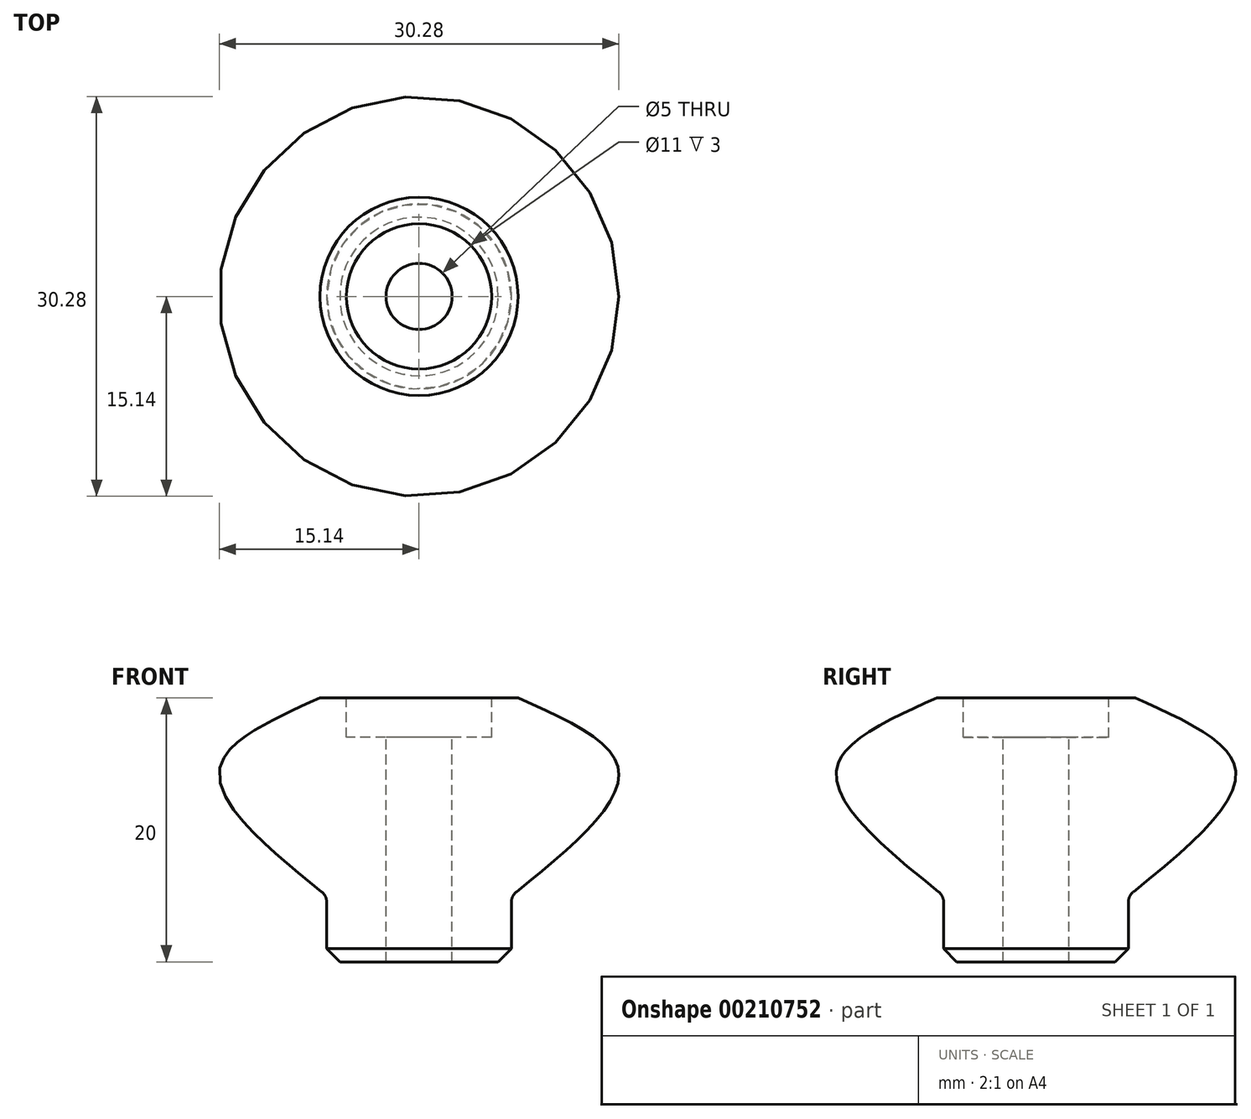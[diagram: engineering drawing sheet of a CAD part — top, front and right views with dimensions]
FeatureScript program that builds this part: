
annotation { "Feature Type Name" : "Feature", "Feature Type Description" : "" }
export const myFeature = defineFeature(function(context is Context, id is Id, definition is map)
    precondition{}
    {
        {
            var Q0;
            Q0=qCreatedBy(makeId("Top.planeOp"),FACE);
            var sketch = newSketch(context, id + "F0", { "sketchPlane" : qUnion([Q0])});
            skCircle(sketch, "E0", {"center": v(0, 0) * mm, "radius": 7 * mm});
            skSolve(sketch);
        }
        {
            var Q0;
            Q0 = qSketchRegion(id + "F0", true);
            extrude(context, id + "F1", {"entities" : qUnion([Q0]), "depth" : 5 * mm});
        }
        {
            var Q0;
            Q0=qCreatedBy(makeId("Top.planeOp"),FACE);
            cPlane(context, id + "F2", {"entities" : qUnion([Q0]), "cplaneType" : CPlaneType.OFFSET, "offset" : 20 * mm, "width" : 150 * mm, "height" : 150 * mm});
        }
        {
            var Q0;
            Q0=qCreatedBy(makeId("Top.planeOp"),FACE);
            cPlane(context, id + "F3", {"entities" : qUnion([Q0]), "cplaneType" : CPlaneType.OFFSET, "offset" : 15 * mm, "width" : 150 * mm, "height" : 150 * mm});
        }
        {
            var Q0;
            Q0=qCreatedBy(id+"F2.planeOp",FACE);
            var sketch = newSketch(context, id + "F4", { "sketchPlane" : qUnion([Q0])});
            skCircle(sketch, "E1", {"center": v(0, 0) * mm, "radius": 7.5 * mm});
            skSolve(sketch);
        }
        {
            var Q0;
            Q0=qCreatedBy(id+"F3.planeOp",FACE);
            var sketch = newSketch(context, id + "F5", { "sketchPlane" : qUnion([Q0])});
            skCircle(sketch, "E2", {"center": v(0, 0) * mm, "radius": 15 * mm});
            skSolve(sketch);
        }
        {
            var Q0;
            Q0=makeQuery(id+"F4.imprint","IMPRINT",FACE,{"disambiguationData":[TD([[makeQuery(id+"F4.imprint","IMPRINT",EDGE,{"derivedFrom":sQuery(id+"F4.wireOp",EDGE,"E1")}),1.0]])]});
            var Q1;
            Q1=makeQuery(id+"F5.imprint","IMPRINT",FACE,{"disambiguationData":[TD([[makeQuery(id+"F5.imprint","IMPRINT",EDGE,{"derivedFrom":sQuery(id+"F5.wireOp",EDGE,"E2")}),1.0]])]});
            var Q2;
            Q2=makeQuery(id+"F1.opExtrude","CAP_FACE",FACE,{"disambiguationData":[OSD([sQuery(id+"F0.wireOp",EDGE,"E0")])],"isStart":false});
            loft(context, id + "F6", {"operationType" : NewBodyOperationType.ADD, "sheetProfilesArray" : [{ "sheetProfileEntities" : qUnion([Q0]) }, { "sheetProfileEntities" : qUnion([Q1]) }, { "sheetProfileEntities" : qUnion([Q2]) }]});
        }
        {
            var Q0;
            Q0=makeQuery(id+"F4.imprint","IMPRINT",FACE,{"disambiguationData":[TD([[makeQuery(id+"F4.imprint","IMPRINT",EDGE,{"derivedFrom":sQuery(id+"F4.wireOp",EDGE,"E1")}),1.0]])]});
            var sketch = newSketch(context, id + "F7", { "sketchPlane" : qUnion([Q0])});
            skCircle(sketch, "E3", {"center": v(0, 0) * mm, "radius": 2.5 * mm});
            skSolve(sketch);
        }
        {
            var Q0;
            Q0 = qSketchRegion(id + "F7", true);
            extrude(context, id + "F8", {"entities" : qUnion([Q0]), "operationType" : NewBodyOperationType.REMOVE, "endBound" : BoundingType.THROUGH_ALL, "oppositeDirection" : true, "depth" : 25 * mm});
        }
        {
            var Q0;
            Q0=makeQuery(id+"F4.imprint","IMPRINT",FACE,{"disambiguationData":[TD([[makeQuery(id+"F4.imprint","IMPRINT",EDGE,{"derivedFrom":sQuery(id+"F4.wireOp",EDGE,"E1")}),1.0]])]});
            var sketch = newSketch(context, id + "F9", { "sketchPlane" : qUnion([Q0])});
            skCircle(sketch, "E4", {"center": v(0, 0) * mm, "radius": 5.5 * mm});
            skSolve(sketch);
        }
        {
            var Q0;
            Q0 = qSketchRegion(id + "F9", true);
            extrude(context, id + "F10", {"entities" : qUnion([Q0]), "operationType" : NewBodyOperationType.REMOVE, "oppositeDirection" : true, "depth" : 3 * mm});
        }
        {
            var Q0;
            {var subQ0=sQuery(id+"F0.wireOp",EDGE,"E0");Q0=makeQuery(id+"F6.boolean.opBoolean","MERGE",EDGE,{"derivedFrom":[makeQuery(id+"F1.opExtrude","CAP_EDGE",EDGE,{"disambiguationData":[OSD([subQ0])],"isStart":false}),makeQuery(id+"F6.opLoft","MID_CAP_EDGE",EDGE,{"disambiguationData":[OSD([subQ0,sQuery(id+"F4.wireOp",EDGE,"E1")])],"capPos":2.0})]});}
            fillet(context, id + "F11", {"entities" : qUnion([Q0]), "radius" : 1 * mm, "tangentPropagation" : true, "allowEdgeOverflow" : false});
        }
        {
            var Q0;
            Q0=makeQuery(id+"F1.opExtrude","CAP_EDGE",EDGE,{"disambiguationData":[OSD([sQuery(id+"F0.wireOp",EDGE,"E0")])],"isStart":true});
            chamfer(context, id + "F12", {"entities" : qUnion([Q0]), "width" : 1 * mm, "tangentPropagation" : true});
        }
    });
